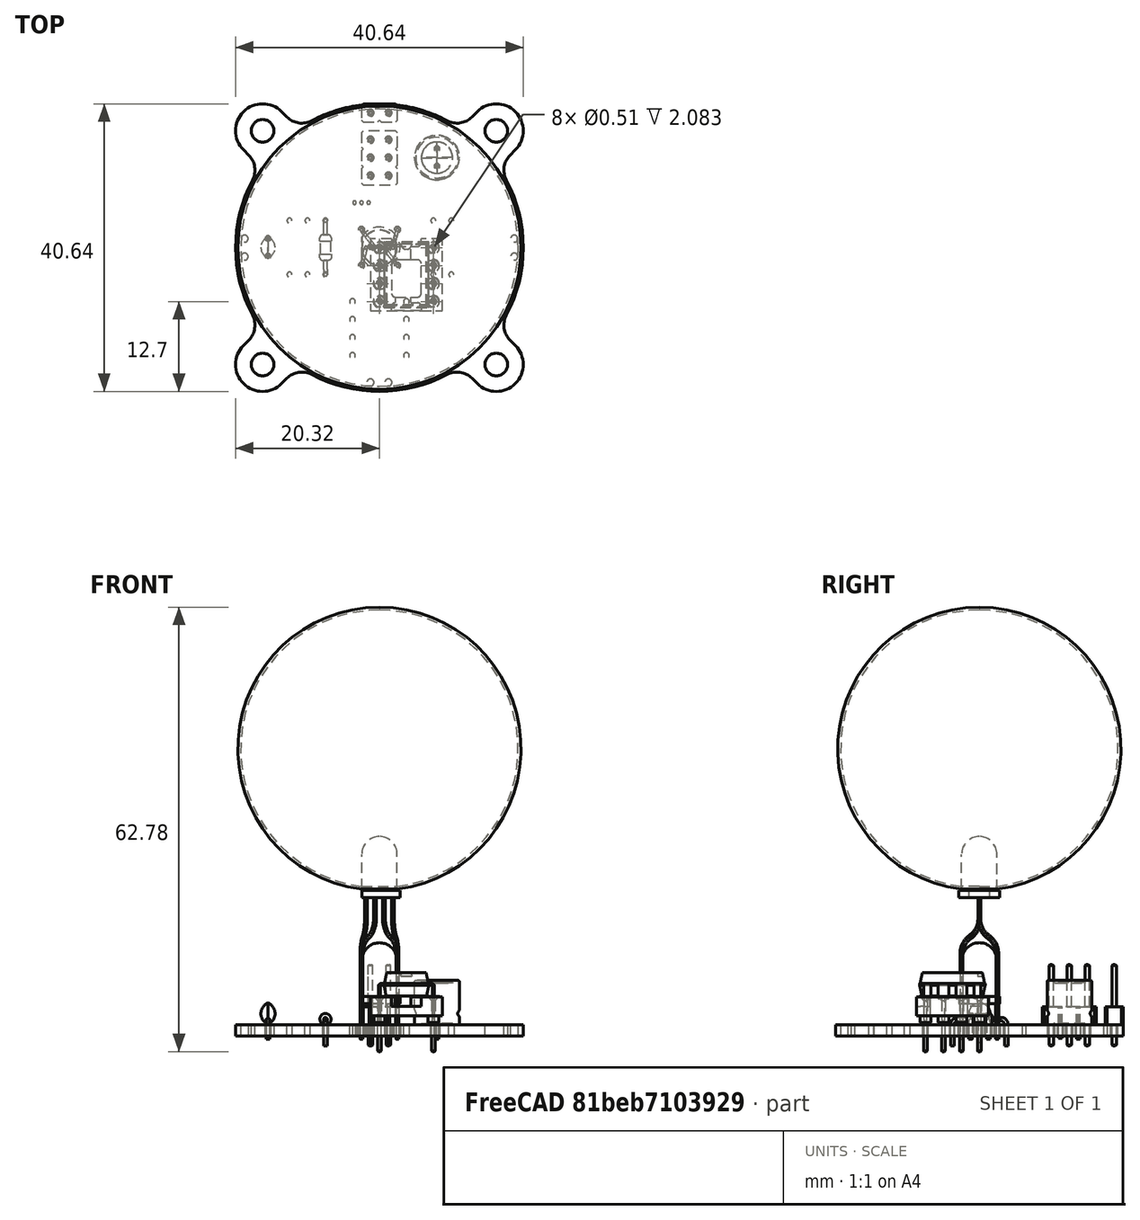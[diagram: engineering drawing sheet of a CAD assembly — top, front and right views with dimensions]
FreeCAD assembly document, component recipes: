
FREECAD ASSEMBLY — COMPONENT RECIPES ("firefly_v1")

This assembly document has 2 components, labeled P0..P1 below (a component is one placed body or linked part). 1 of them carries a construction recipe — the FreeCAD feature program that regenerates the part from scratch, quoted from this document or its linked companion documents; the rest are supplied as boundary geometry only. No exploded tour is included for this assembly.
COMPONENT P0 — geometry summary ("firefly"; no construction recipe available for this part):
  bounding box: 40.6 x 40.6 x 30.4 mm
  tessellated surface: 223,748 triangles
  volume: 2649 mm^3 (5% of its bounding box)
COMPONENT P1 — recipe-attached ("Body001", modeled in this document).
Construction recipe (the document's own serialized feature program — sketch geometry with constraints, then the solid features built on it; lengths are millimeters unless a unit is written):

FEATURE [Sketcher::SketchObject] Sketch
  ArcFitTolerance = 1e-06
  AttachmentSupport = -> [XZ_Plane010]
  FullyConstrained = true
  MapMode = 5
  Placement = pos=(0,0,0) rot=(1,0,0;1.5708rad)
  Support = -> [XZ_Plane010]
  TreeRank = 12
  sketch-geometry (4):
    g0: ArcOfCircle CenterX=0 CenterY=39 CenterZ=0 NormalX=0 NormalY=0 NormalZ=1 AngleXU=0 Radius=20 StartAngle=1.5708 EndAngle=4.71239
    g1: ArcOfCircle CenterX=0 CenterY=39 CenterZ=0 NormalX=0 NormalY=0 NormalZ=1 AngleXU=0 Radius=19.6 StartAngle=1.5708 EndAngle=4.71239
    g2: LineSegment StartX=0 StartY=59 StartZ=0 EndX=0 EndY=58.6 EndZ=0
    g3: LineSegment StartX=0 StartY=19 StartZ=0 EndX=0 EndY=19.4 EndZ=0
  constraints (13):
    c: PointOnObject(g0,g-2)
    c: PointOnObject(g0,g-2)
    c: Radius(g0) = 20
    c: Coincident(g1,g0)
    c: Coincident(g2,g0)
    c: Coincident(g2,g1)
    c: Vertical(g2)
    c: Coincident(g3,g0)
    c: Coincident(g3,g1)
    c: PointOnObject(g0,g-2)
    c: Vertical(g3)
    c: DistanceY(g2,g2) = 0.4
    c: DistanceY(g-1,g0) = 39
FEATURE [PartDesign::Revolution] Revolution
  Angle = 360
  Axis = (0,2e-16,1)
  Base = (0,0,0)
  ClaimChildren = false
  Fit = 0
  FitJoin = 0
  InnerFit = 0
  InnerFitJoin = 0
  NewSolid = false
  Placement = pos=(0,0,0) rot=(1,0,0;1.5708rad)
  Profile = -> Sketch
  ReferenceAxis = -> Sketch [V_Axis]
  Suppress = false
  TreeRank = 13
  _ProfileBasedVersion = 1
FEATURE [Sketcher::SketchObject] Sketch001
  ArcFitTolerance = 1e-06
  FullyConstrained = true
  TreeRank = 14
  sketch-geometry (1):
    g0: Circle CenterX=0 CenterY=0 CenterZ=0 NormalX=0 NormalY=0 NormalZ=1 AngleXU=0 Radius=2.5
  constraints (2):
    c: Coincident(g0,g-1)
    c: Diameter(g0) = 5
FEATURE [PartDesign::Pocket] Pocket
  BaseFeature = -> Revolution
  ClaimChildren = false
  ColoredElements = -> Pocket [Face1,Face3]
  Fit = 0
  FitJoin = 0
  InnerFit = 0
  InnerFitJoin = 0
  InnerTaperAngle = 0
  InnerTaperAngleRev = 0
  Length = 20
  Length2 = 100
  Linearize = true
  NewSolid = false
  Placement = pos=(0,0,0) rot=(1,0,0;1.5708rad)
  Profile = -> Sketch001
  Reversed = true
  Suppress = false
  TreeRank = 15
  Type = 0
  _ProfileBasedVersion = 1
FEATURE [PartDesign::Body] Body  label="Body001"
  AutoGroupSolids = false
  ClaimAllChildren = false
  ExportMode = 0
  Group = -> [Sketch,Revolution,Sketch001,Pocket]
  Origin = -> Origin010
  Tip = -> Pocket
  TreeRank = 11
  _ExportChildren = -> [Revolution,Pocket]
  _GroupVersion = 1
PROVENANCE & LICENSES
A FreeCAD (.FCStd) document from a public repository crawl; recipes are the document's own serialized feature recipes (and, for linked parts, companion documents' recipes).
License: gpl-3.0.
